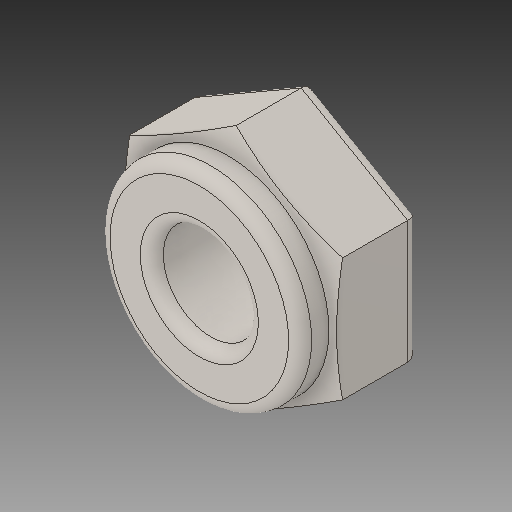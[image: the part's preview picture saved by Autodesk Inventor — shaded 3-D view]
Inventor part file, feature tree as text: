
AUTODESK INVENTOR PART (.ipt)
format: ipt  version: 2018 (Build 220112000, 112)  size: 158,720 bytes
history: native  units: in
note: dims shown in document units (in); Inventor stores cm internally (conversion verified against a paired STEP export)
features: fillet x1
ambient origin geometry x8: Origin, YZ Plane, XZ Plane, XY Plane, X Axis, Y Axis, Z Axis, Center Point
bodies: Solid1 (feature_tree)
feature tree (1):
  fillet  "Fillet4"  [1 undecoded]
note: 1 required parameter value undecoded (feature->parameter linkage not recoverable at this tier; creation-order binding heuristic only, values carry confidence <= 0.55)
